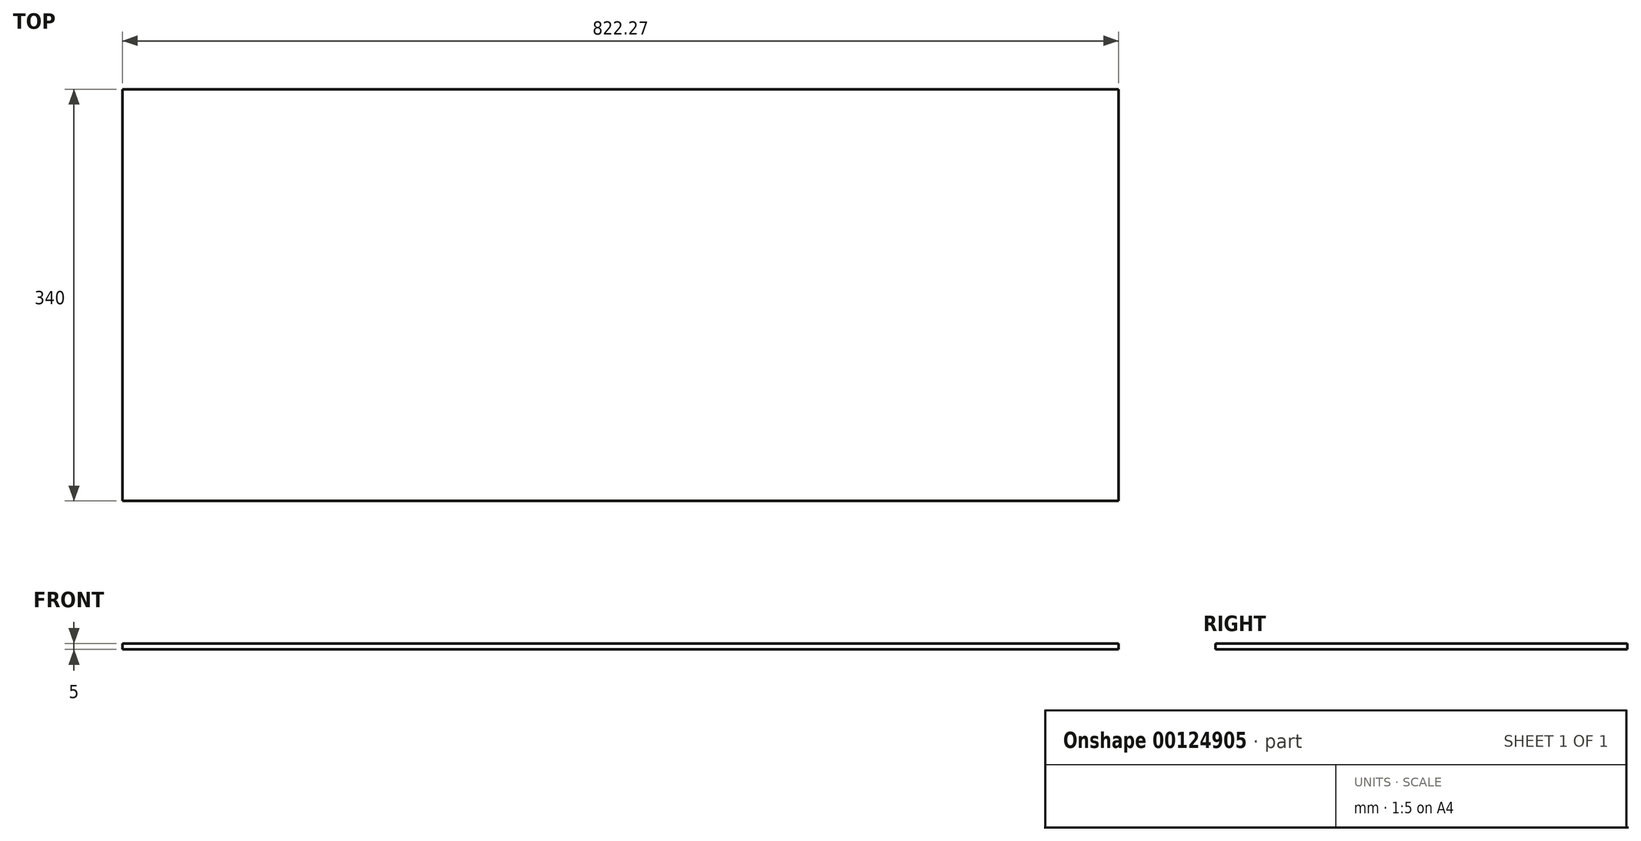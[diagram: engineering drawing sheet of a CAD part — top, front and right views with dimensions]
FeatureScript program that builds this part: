
annotation { "Feature Type Name" : "Feature", "Feature Type Description" : "" }
export const myFeature = defineFeature(function(context is Context, id is Id, definition is map)
    precondition{}
    {
        {
            var Q0;
            Q0=qCreatedBy(makeId("Top.planeOp"),FACE);
            var sketch = newSketch(context, id + "F0", { "sketchPlane" : qUnion([Q0])});
            skPoint(sketch, "E0.middle", {"position": v(0, 0) * mm});
            skLineSegment(sketch, "E1.top", {"start": v(557.5, 0) * mm, "end": v(278.18, 0) * mm});
            skLineSegment(sketch, "E1.left", {"start": v(557.5, 340) * mm, "end": v(557.5, 0) * mm});
            skLineSegment(sketch, "E1.right", {"start": v(278.18, 340) * mm, "end": v(278.18, 0) * mm});
            skLineSegment(sketch, "E2.bottom", {"start": v(278.18, 340) * mm, "end": v(108.18, 340) * mm});
            skLineSegment(sketch, "E2.top", {"start": v(278.18, 0) * mm, "end": v(108.18, 0) * mm});
            skLineSegment(sketch, "E2.right", {"start": v(108.18, 340) * mm, "end": v(108.18, 0) * mm});
            skLineSegment(sketch, "E3.bottom", {"start": v(108.18, 340) * mm, "end": v(-2.82, 340) * mm});
            skLineSegment(sketch, "E3.top", {"start": v(108.18, 0) * mm, "end": v(-2.82, 0) * mm});
            skLineSegment(sketch, "E3.right", {"start": v(-2.82, 340) * mm, "end": v(-2.82, 0) * mm});
            skLineSegment(sketch, "E4", {"start": v(278.18, 340) * mm, "end": v(557.5, 340) * mm});
            skLineSegment(sketch, "E5.bottom", {"start": v(-57.23, 340) * mm, "end": v(-2.82, 340) * mm});
            skLineSegment(sketch, "E6.bottom", {"start": v(557.5, 340) * mm, "end": v(577.97, 340) * mm});
            skLineSegment(sketch, "E6.top", {"start": v(557.5, 0) * mm, "end": v(577.97, 0) * mm});
            skLineSegment(sketch, "E6.right", {"start": v(577.97, 340) * mm, "end": v(577.97, 0) * mm});
            skLineSegment(sketch, "E7.bottom", {"start": v(-2.82, 340) * mm, "end": v(-42.57, 340) * mm});
            skLineSegment(sketch, "E7.top", {"start": v(-2.82, 0) * mm, "end": v(-42.57, 0) * mm});
            skLineSegment(sketch, "E7.right", {"start": v(-42.57, 340) * mm, "end": v(-42.57, 0) * mm});
            skLineSegment(sketch, "E8.bottom", {"start": v(-42.57, 340) * mm, "end": v(-80.44, 340) * mm});
            skLineSegment(sketch, "E8.top", {"start": v(-42.57, 0) * mm, "end": v(-80.44, 0) * mm});
            skLineSegment(sketch, "E8.right", {"start": v(-80.44, 340) * mm, "end": v(-80.44, 0) * mm});
            skLineSegment(sketch, "E9.bottom", {"start": v(-80.44, 0) * mm, "end": v(-162.37, 0) * mm});
            skLineSegment(sketch, "E9.top", {"start": v(-80.44, 291) * mm, "end": v(-162.37, 291) * mm});
            skLineSegment(sketch, "E9.left", {"start": v(-80.44, 0) * mm, "end": v(-80.44, 291) * mm});
            skLineSegment(sketch, "E9.right", {"start": v(-162.37, 0) * mm, "end": v(-162.37, 291) * mm});
            skLineSegment(sketch, "E10.bottom", {"start": v(-162.37, 291) * mm, "end": v(-244.3, 291) * mm});
            skLineSegment(sketch, "E10.top", {"start": v(-162.37, 0) * mm, "end": v(-244.3, 0) * mm});
            skLineSegment(sketch, "E10.left", {"start": v(-162.37, 291) * mm, "end": v(-162.37, 0) * mm});
            skLineSegment(sketch, "E10.right", {"start": v(-244.3, 291) * mm, "end": v(-244.3, 0) * mm});
            skLineSegment(sketch, "E11", {"start": v(-80.44, 340) * mm, "end": v(-244.3, 340) * mm});
            skLineSegment(sketch, "E12", {"start": v(-244.3, 340) * mm, "end": v(-244.3, 291) * mm});
            skLineSegment(sketch, "E13", {"start": v(-244.3, 340) * mm, "end": v(-244.3, 0) * mm});
            skLineSegment(sketch, "E14", {"start": v(-244.3, 0) * mm, "end": v(577.97, 0) * mm});
            skLineSegment(sketch, "E15", {"start": v(-244.3, 340) * mm, "end": v(577.97, 340) * mm});
            skLineSegment(sketch, "E16", {"start": v(577.97, 0) * mm, "end": v(577.97, 340) * mm});
            skLineSegment(sketch, "E17", {"start": v(-162.37, 0) * mm, "end": v(-80.44, 0) * mm});
            skSolve(sketch);
        }
        {
            var Q0;
            Q0 = qSketchRegion(id + "F0", true);
            extrude(context, id + "F1", {"entities" : qUnion([Q0]), "depth" : 5 * mm});
        }
    });
